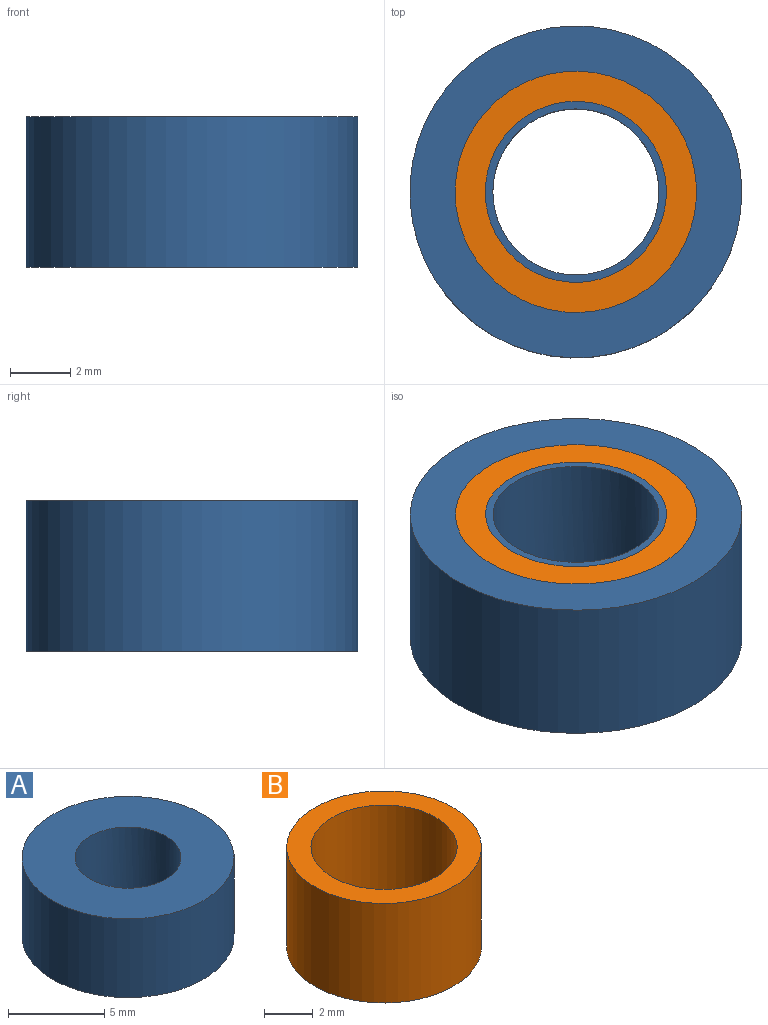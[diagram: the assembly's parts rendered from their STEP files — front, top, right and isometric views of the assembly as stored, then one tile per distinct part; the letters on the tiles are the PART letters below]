
ASSEMBLY  parts=2 mates=1
PART A: 4 faces, bbox 11x11x5 mm
  f0: cylinder r=5.5mm len=11mm, axis (0,0,-1), area 172.8mm2, adj f1,f2
  f1: plane 11x11mm, normal (0,0,1), area 71.3mm2, adj f0,f3
  f2: plane 11x11mm, normal (0,0,-1), area 71.3mm2, adj f0,f3
  f3: cylinder r=2.75mm len=5.5mm, axis (0,0,-1), area 86.4mm2, adj f1,f2
PART B: 4 faces, bbox 8x8x5 mm
  f0: cylinder r=3mm len=6mm, axis (0,0,-1), area 94.2mm2, adj f2,f3
  f1: cylinder r=4mm len=8mm, axis (0,0,-1), area 125.7mm2, adj f2,f3
  f2: plane 8x8mm, normal (0,0,1), area 22mm2, adj f0,f1
  f3: plane 8x8mm, normal (0,0,-1), area 22mm2, adj f0,f1
PLACE A t=(-4.79,0.15,1.53)mm
PLACE B rot(axis=(0,0,-1),145deg) t=(-4.79,0.15,1.53)mm
MATE revolute B.f0 <-> A.f0  axis (0,0,-1) through (-4.79,0.15,1.53)mm
